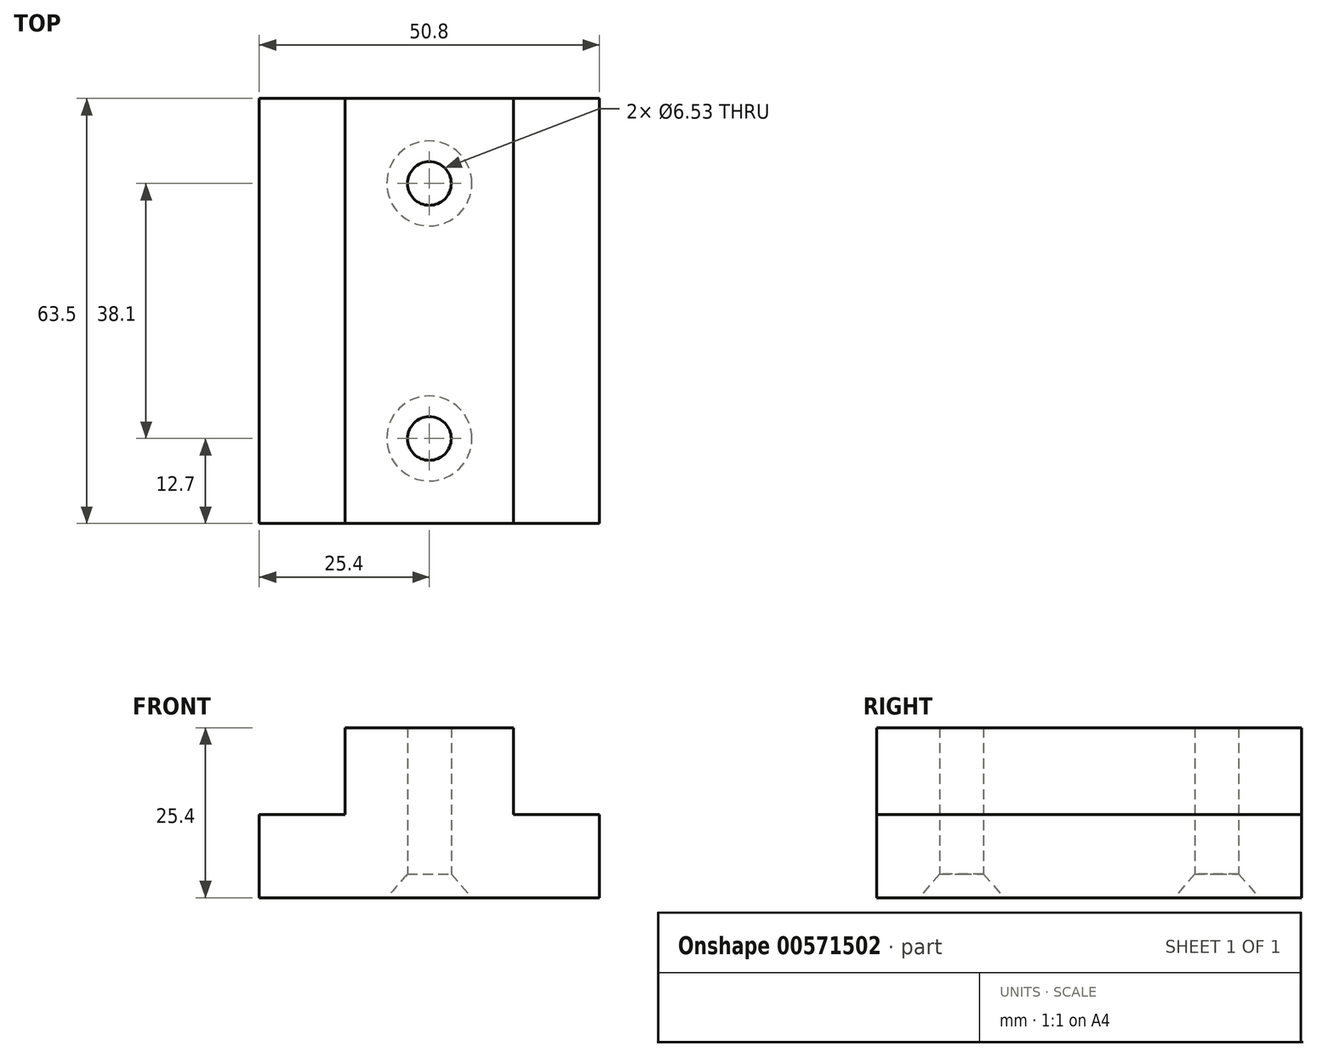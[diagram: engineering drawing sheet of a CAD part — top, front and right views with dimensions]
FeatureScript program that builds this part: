
annotation { "Feature Type Name" : "Feature", "Feature Type Description" : "" }
export const myFeature = defineFeature(function(context is Context, id is Id, definition is map)
    precondition{}
    {
        {
            var Q0;
            Q0=qCreatedBy(makeId("Front.planeOp"),FACE);
            var sketch = newSketch(context, id + "F0", { "sketchPlane" : qUnion([Q0])});
            skLineSegment(sketch, "E0.bottom", {"start": v(0, 0) * mm, "end": v(50.8, 0) * mm});
            skLineSegment(sketch, "E0.top", {"start": v(0, 12.45) * mm, "end": v(12.83, 12.45) * mm});
            skLineSegment(sketch, "E0.left", {"start": v(0, 0) * mm, "end": v(0, 12.45) * mm});
            skLineSegment(sketch, "E0.right", {"start": v(50.8, 0) * mm, "end": v(50.8, 12.45) * mm});
            skPoint(sketch, "E1", {"position": v(25.4, 12.45) * mm});
            skLineSegment(sketch, "E2.top", {"start": v(12.83, 25.4) * mm, "end": v(37.97, 25.4) * mm});
            skLineSegment(sketch, "E2.left", {"start": v(12.83, 12.45) * mm, "end": v(12.83, 25.4) * mm});
            skLineSegment(sketch, "E2.right", {"start": v(37.97, 12.45) * mm, "end": v(37.97, 25.4) * mm});
            skLineSegment(sketch, "E3.trimOffspring", {"start": v(37.97, 12.45) * mm, "end": v(50.8, 12.45) * mm});
            skSolve(sketch);
        }
        {
            var Q0;
            Q0=makeQuery(id+"F0.imprint","IMPRINT",FACE,{"disambiguationData":[TD([[makeQuery(id+"F0.imprint","IMPRINT",EDGE,{"derivedFrom":sQuery(id+"F0.wireOp",EDGE,"E0.bottom")}),1.0]])]});
            extrude(context, id + "F1", {"entities" : qUnion([Q0]), "depth" : 63.5 * mm, "offsetDistance" : 25.4 * mm});
        }
        {
            var Q0;
            Q0=makeQuery(id+"F1.opExtrude","SWEPT_FACE",FACE,{"disambiguationData":[OSD([sQuery(id+"F0.wireOp",EDGE,"E0.bottom")])]});
            var sketch = newSketch(context, id + "F2", { "sketchPlane" : qUnion([Q0])});
            skPoint(sketch, "E4", {"position": v(25.4, 50.8) * mm});
            skPoint(sketch, "E4.positionSnap0", {"position": v(25.4, 63.5) * mm});
            skPoint(sketch, "E5", {"position": v(25.4, 12.7) * mm});
            skSolve(sketch);
        }
        {
            var Q0;
            Q0=sQuery(id+"F2.wireOp",VERTEX,"E4");
            var Q1;
            Q1=sQuery(id+"F2.wireOp",VERTEX,"E5");
            var Q2;
            Q2=makeQuery(id+"F1.opExtrude","SWEPT_BODY",BODY,{"disambiguationData":[OSD([sQuery(id+"F0.wireOp",EDGE,"E0.bottom"),sQuery(id+"F0.wireOp",EDGE,"E0.top"),sQuery(id+"F0.wireOp",EDGE,"E0.left"),sQuery(id+"F0.wireOp",EDGE,"E0.right"),sQuery(id+"F0.wireOp",EDGE,"E2.top"),sQuery(id+"F0.wireOp",EDGE,"E2.left"),sQuery(id+"F0.wireOp",EDGE,"E2.right"),sQuery(id+"F0.wireOp",EDGE,"E3.trimOffspring")])]});
            hole(context, id + "F3", {"style" : HoleStyle.C_SINK, "endStyle" : HoleEndStyle.THROUGH, "holeDiameter" : 6.53 * mm, "cSinkDiameter" : 12.7 * mm, "cSinkAngle" : 82 * degree, "isTappedThrough" : true, "tappedDepth" : 12.7 * mm, "tapClearance" : 3, "locations" : qUnion([Q0, Q1]), "scope" : qUnion([Q2])});
        }
    });
